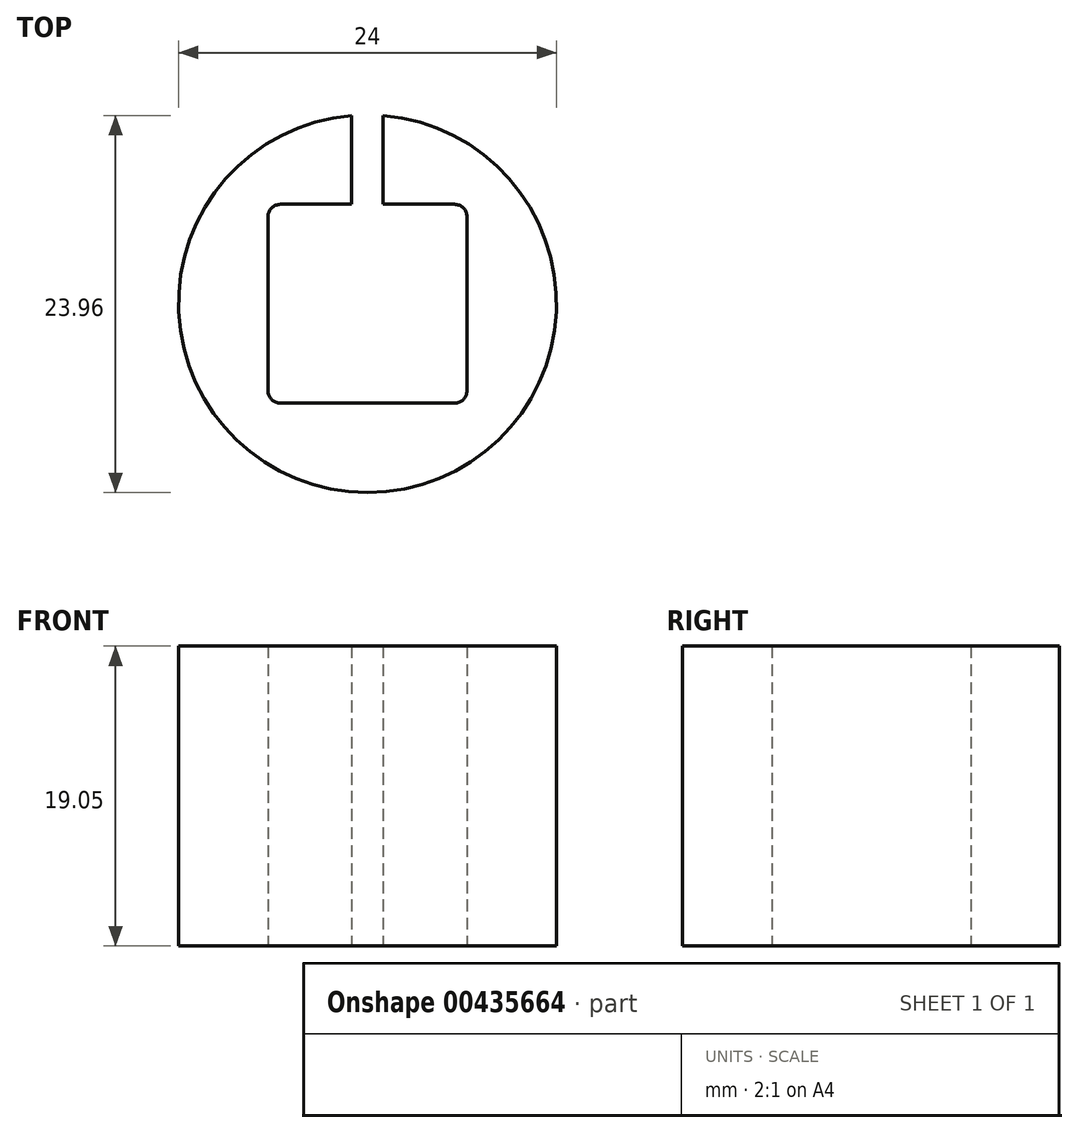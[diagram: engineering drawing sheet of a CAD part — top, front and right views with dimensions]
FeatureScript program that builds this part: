
annotation { "Feature Type Name" : "Feature", "Feature Type Description" : "" }
export const myFeature = defineFeature(function(context is Context, id is Id, definition is map)
    precondition{}
    {
        {
            var Q0;
            Q0=qCreatedBy(makeId("Top.planeOp"),FACE);
            var sketch = newSketch(context, id + "F0", { "sketchPlane" : qUnion([Q0])});
            skArc(sketch, "E0", {"start": v(-1, 11.96) * mm, "mid": v(0, -12) * mm, "end": v(1, 11.96) * mm});
            skLineSegment(sketch, "E1.bottom", {"start": v(-6.32, 6.32) * mm, "end": v(-1, 6.32) * mm});
            skLineSegment(sketch, "E1.top", {"start": v(-6.32, -6.32) * mm, "end": v(6.32, -6.32) * mm});
            skLineSegment(sketch, "E1.left", {"start": v(-6.32, 6.32) * mm, "end": v(-6.32, -6.32) * mm});
            skLineSegment(sketch, "E1.right", {"start": v(6.32, 6.32) * mm, "end": v(6.32, -6.32) * mm});
            skLineSegment(sketch, "E2", {"start": v(-6.32, 6.32) * mm, "end": v(6.32, -6.32) * mm, "construction": true});
            skLineSegment(sketch, "E3", {"start": v(-1, 11.96) * mm, "end": v(-1, 6.32) * mm});
            skLineSegment(sketch, "E4", {"start": v(1, 11.96) * mm, "end": v(1, 6.32) * mm});
            skLineSegment(sketch, "E5.trimOffspring", {"start": v(1, 6.32) * mm, "end": v(6.32, 6.32) * mm});
            skSolve(sketch);
        }
        {
            var Q0;
            Q0=makeQuery(id+"F0.imprint","IMPRINT",FACE,{"disambiguationData":[TD([[makeQuery(id+"F0.imprint","IMPRINT",EDGE,{"derivedFrom":sQuery(id+"F0.wireOp",EDGE,"E0")}),1.0]])]});
            extrude(context, id + "F1", {"entities" : qUnion([Q0]), "depth" : 19.05 * mm});
        }
        {
            var Q0;
            Q0=makeQuery(id+"F1.opExtrude","SWEPT_EDGE",EDGE,{"disambiguationData":[OSD([sQuery(id+"F0.wireOp",EDGE,"E1.bottom"),sQuery(id+"F0.wireOp",EDGE,"E1.left")])]});
            var Q1;
            Q1=makeQuery(id+"F1.opExtrude","SWEPT_EDGE",EDGE,{"disambiguationData":[OSD([sQuery(id+"F0.wireOp",EDGE,"E1.right"),sQuery(id+"F0.wireOp",EDGE,"E5.trimOffspring")])]});
            var Q2;
            Q2=makeQuery(id+"F1.opExtrude","SWEPT_EDGE",EDGE,{"disambiguationData":[OSD([sQuery(id+"F0.wireOp",EDGE,"E1.top"),sQuery(id+"F0.wireOp",EDGE,"E1.right")])]});
            var Q3;
            Q3=makeQuery(id+"F1.opExtrude","SWEPT_EDGE",EDGE,{"disambiguationData":[OSD([sQuery(id+"F0.wireOp",EDGE,"E1.top"),sQuery(id+"F0.wireOp",EDGE,"E1.left")])]});
            fillet(context, id + "F2", {"entities" : qUnion([Q0, Q1, Q2, Q3]), "radius" : 0.8 * mm, "tangentPropagation" : true, "allowEdgeOverflow" : false});
        }
    });
